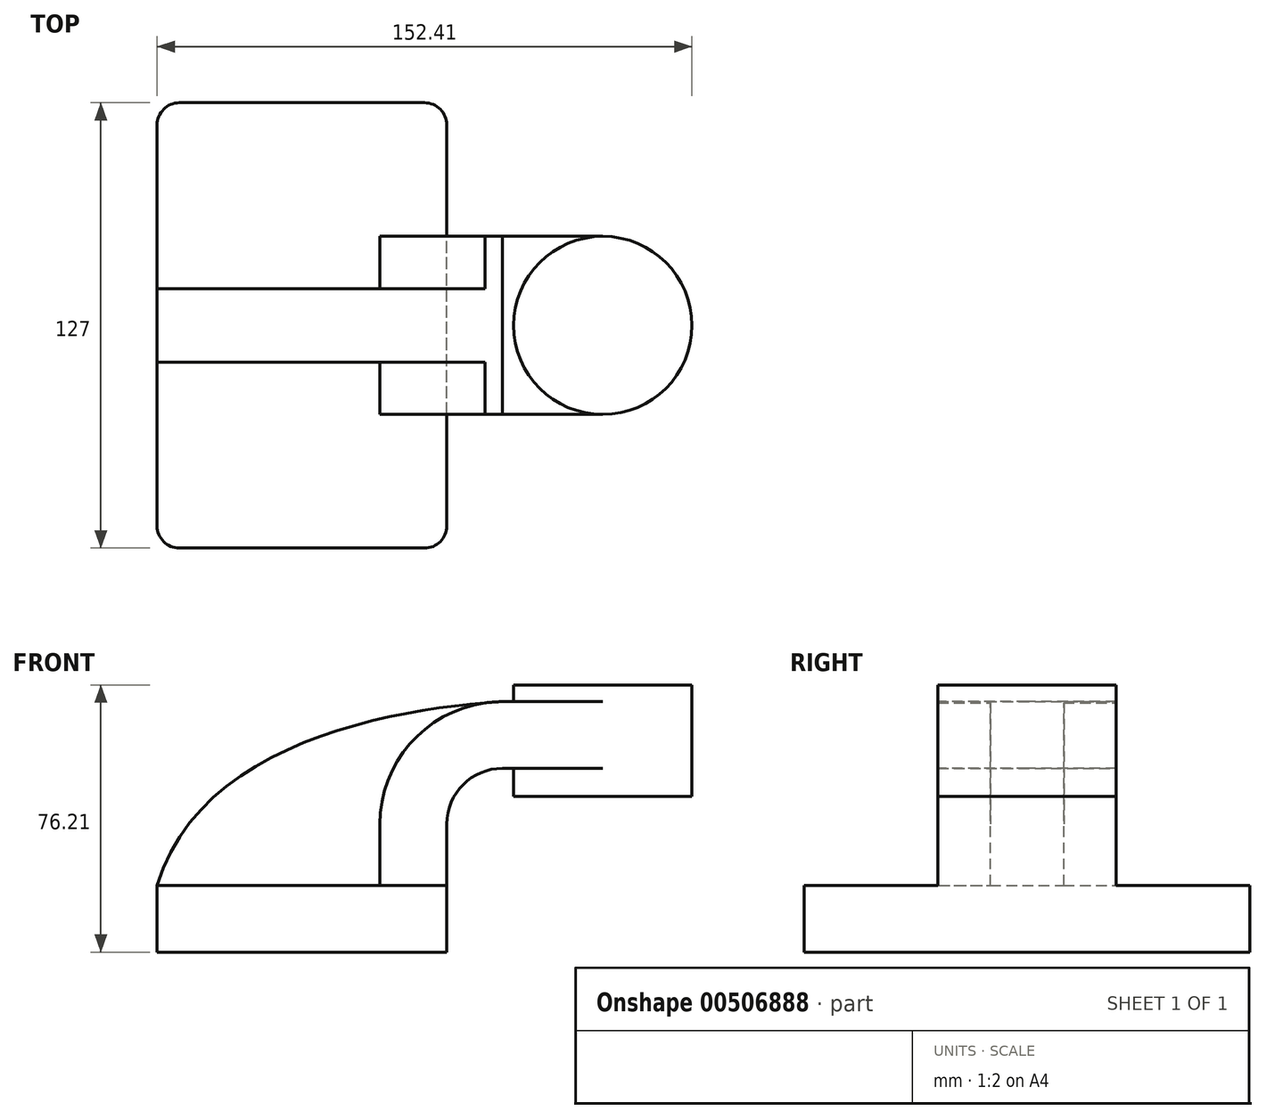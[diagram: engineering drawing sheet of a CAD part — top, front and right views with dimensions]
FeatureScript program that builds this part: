
annotation { "Feature Type Name" : "Feature", "Feature Type Description" : "" }
export const myFeature = defineFeature(function(context is Context, id is Id, definition is map)
    precondition{}
    {
        {
            var Q0;
            Q0=qCreatedBy(makeId("Front.planeOp"),FACE);
            var sketch = newSketch(context, id + "F0", { "sketchPlane" : qUnion([Q0])});
            skLineSegment(sketch, "E0.bottom", {"start": v(41.27, 9.53) * mm, "end": v(-41.27, 9.53) * mm});
            skLineSegment(sketch, "E0.top", {"start": v(41.27, -9.52) * mm, "end": v(-41.27, -9.52) * mm});
            skLineSegment(sketch, "E0.left", {"start": v(41.27, 9.53) * mm, "end": v(41.27, -9.52) * mm});
            skLineSegment(sketch, "E0.right", {"start": v(-41.27, 9.53) * mm, "end": v(-41.27, -9.52) * mm});
            skPoint(sketch, "E0.middle", {"position": v(0, 0) * mm});
            skLineSegment(sketch, "E1.bottom", {"start": v(111.13, 66.68) * mm, "end": v(60.33, 66.68) * mm});
            skLineSegment(sketch, "E1.top", {"start": v(111.13, 34.92) * mm, "end": v(60.33, 34.92) * mm});
            skLineSegment(sketch, "E1.left", {"start": v(111.13, 66.68) * mm, "end": v(111.13, 34.93) * mm});
            skLineSegment(sketch, "E1.right", {"start": v(60.33, 66.68) * mm, "end": v(60.33, 34.93) * mm});
            skPoint(sketch, "E1.middle", {"position": v(85.73, 50.8) * mm});
            skLineSegment(sketch, "E2", {"start": v(41.27, 9.53) * mm, "end": v(41.27, 27) * mm});
            skArc(sketch, "E3", {"start": v(41.28, 27) * mm, "mid": v(45.92, 38.23) * mm, "end": v(57.15, 42.88) * mm});
            skLineSegment(sketch, "E4", {"start": v(57.15, 42.88) * mm, "end": v(85.73, 42.88) * mm});
            skPoint(sketch, "E4.endSnap0", {"position": v(85.73, 34.93) * mm});
            skLineSegment(sketch, "E5.0", {"start": v(57.15, 61.93) * mm, "end": v(85.73, 61.93) * mm});
            skArc(sketch, "E5.1", {"start": v(22.22, 27) * mm, "mid": v(32.45, 51.7) * mm, "end": v(57.15, 61.93) * mm});
            skLineSegment(sketch, "E5.2", {"start": v(22.22, 9.53) * mm, "end": v(22.22, 27) * mm});
            skLineSegment(sketch, "E6", {"start": v(85.73, 34.93) * mm, "end": v(85.73, 66.68) * mm});
            skFitSpline(sketch, "E7", {"points": [v(-41.28, 9.53) * mm, v(57.15, 61.93) * mm], "startDerivative": vector(36.55, 123.47) * mm, "endDerivative": vector(90.48, 5.58) * mm});
            skSolve(sketch);
        }
        {
            var Q0;
            Q0=makeQuery(id+"F0.imprint","IMPRINT",FACE,{"disambiguationData":[TD([[makeQuery(id+"F0.imprint","IMPRINT",EDGE,{"derivedFrom":sQuery(id+"F0.wireOp",EDGE,"E0.top")}),-1.0]])]});
            extrude(context, id + "F1", {"entities" : qUnion([Q0]), "endBound" : BoundingType.SYMMETRIC, "depth" : 127 * mm});
        }
        {
            var Q0;
            {var subQ1=sQuery(id+"F0.wireOp",EDGE,"E2");Q0=makeQuery(id+"F0.imprint","IMPRINT",FACE,{"disambiguationData":[TD([[makeQuery(id+"F0.imprint","IMPRINT",EDGE,{"derivedFrom":subQ1}),1.0]])]});}
            var Q1;
            {var subQ0=sQuery(id+"F0.wireOp",EDGE,"E5.0");var subQ1=sQuery(id+"F0.wireOp",EDGE,"E1.right");var subQ2=makeQuery(id+"F0.imprint","INTERSECT",VERTEX,{"derivedFrom":[subQ1,subQ0]});Q1=makeQuery(id+"F0.imprint","IMPRINT",FACE,{"disambiguationData":[TD([[makeQuery(id+"F0.imprint","IMPRINT",EDGE,{"disambiguationData":[TD([[subQ2,-1.0]])],"derivedFrom":subQ1}),1.0]])]});}
            extrude(context, id + "F2", {"entities" : qUnion([Q0, Q1]), "operationType" : NewBodyOperationType.ADD, "endBound" : BoundingType.SYMMETRIC, "depth" : 50.8 * mm});
        }
        {
            var Q0;
            {var subQ0=sQuery(id+"F0.wireOp",EDGE,"E1.left");Q0=makeQuery(id+"F0.imprint","IMPRINT",FACE,{"disambiguationData":[TD([[makeQuery(id+"F0.imprint","IMPRINT",EDGE,{"derivedFrom":subQ0}),-1.0]])]});}
            var Q1;
            Q1=sQuery(id+"F0.wireOp",EDGE,"E6");
            revolve(context, id + "F3", {"operationType" : NewBodyOperationType.ADD, "entities" : qUnion([Q0]), "axis" : qUnion([Q1]), "revolveType" : RevolveType.FULL});
        }
        {
            var Q0;
            Q0=makeQuery(id+"F1.opExtrude","CAP_EDGE",EDGE,{"disambiguationData":[OSD([sQuery(id+"F0.wireOp",EDGE,"E0.left")])],"isStart":false});
            var Q1;
            Q1=makeQuery(id+"F1.opExtrude","CAP_EDGE",EDGE,{"disambiguationData":[OSD([sQuery(id+"F0.wireOp",EDGE,"E0.right")])],"isStart":false});
            var Q2;
            Q2=makeQuery(id+"F1.opExtrude","CAP_EDGE",EDGE,{"disambiguationData":[OSD([sQuery(id+"F0.wireOp",EDGE,"E0.left")])],"isStart":true});
            var Q3;
            Q3=makeQuery(id+"F1.opExtrude","CAP_EDGE",EDGE,{"disambiguationData":[OSD([sQuery(id+"F0.wireOp",EDGE,"E0.right")])],"isStart":true});
            fillet(context, id + "F4", {"entities" : qUnion([Q0, Q1, Q2, Q3]), "radius" : 6.35 * mm, "tangentPropagation" : true, "allowEdgeOverflow" : false});
        }
        {
            var Q0;
            {var subQ3=sQuery(id+"F0.wireOp",EDGE,"E5.2");Q0=makeQuery(id+"F0.imprint","IMPRINT",FACE,{"disambiguationData":[TD([[makeQuery(id+"F0.imprint","IMPRINT",EDGE,{"derivedFrom":subQ3}),1.0]])]});}
            extrude(context, id + "F5", {"entities" : qUnion([Q0]), "operationType" : NewBodyOperationType.ADD, "endBound" : BoundingType.SYMMETRIC, "depth" : 20.95 * mm});
        }
    });
